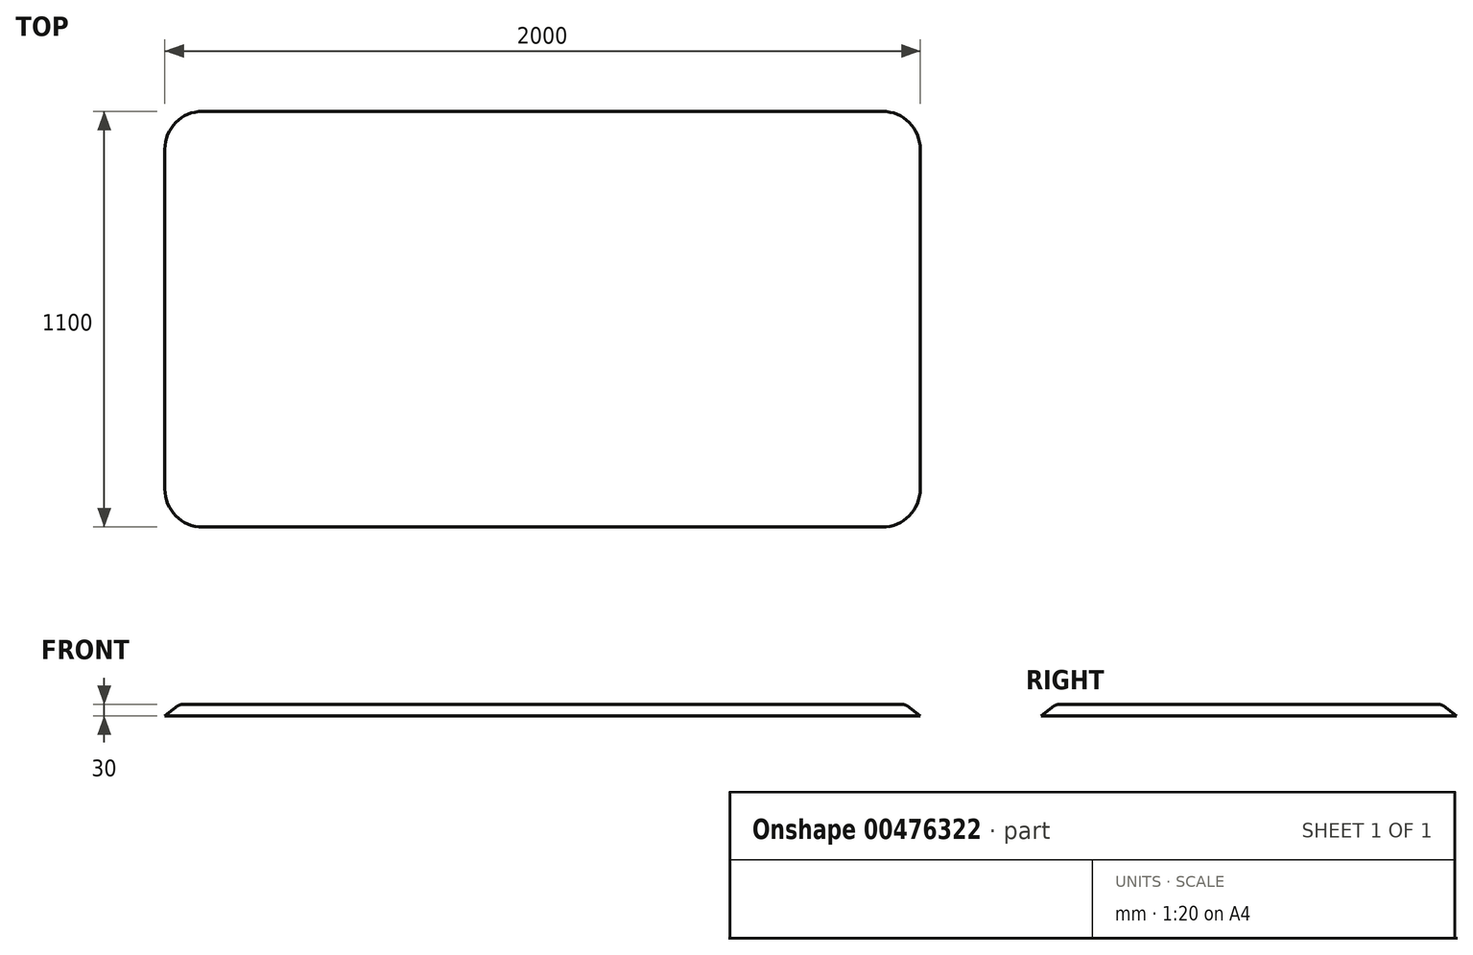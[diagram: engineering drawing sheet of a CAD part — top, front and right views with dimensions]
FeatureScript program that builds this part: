
annotation { "Feature Type Name" : "Feature", "Feature Type Description" : "" }
export const myFeature = defineFeature(function(context is Context, id is Id, definition is map)
    precondition{}
    {
        {
            var Q0;
            Q0=qCreatedBy(makeId("Top.planeOp"),FACE);
            var sketch = newSketch(context, id + "F0", { "sketchPlane" : qUnion([Q0])});
            skLineSegment(sketch, "E0.bottom", {"start": v(950, 500) * mm, "end": v(-950, 500) * mm});
            skLineSegment(sketch, "E0.top", {"start": v(950, -500) * mm, "end": v(-950, -500) * mm});
            skLineSegment(sketch, "E0.left", {"start": v(950, 500) * mm, "end": v(950, -500) * mm});
            skLineSegment(sketch, "E0.right", {"start": v(-950, 500) * mm, "end": v(-950, -500) * mm});
            skPoint(sketch, "E0.middle", {"position": v(0, 0) * mm});
            skSolve(sketch);
        }
        {
            var Q0;
            Q0=qSketchRegion(id+"F0",true);
            extrude(context, id + "F1", {"entities" : qUnion([Q0]), "depth" : 30 * mm});
        }
        {
            var Q0;
            Q0=makeQuery(id+"F1.opExtrude","SWEPT_EDGE",EDGE,{"disambiguationData":[OSD([sQuery(id+"F0.wireOp",EDGE,"E0.top"),sQuery(id+"F0.wireOp",EDGE,"E0.right")])]});
            var Q1;
            Q1=makeQuery(id+"F1.opExtrude","SWEPT_EDGE",EDGE,{"disambiguationData":[OSD([sQuery(id+"F0.wireOp",EDGE,"E0.bottom"),sQuery(id+"F0.wireOp",EDGE,"E0.right")])]});
            var Q2;
            Q2=makeQuery(id+"F1.opExtrude","SWEPT_EDGE",EDGE,{"disambiguationData":[OSD([sQuery(id+"F0.wireOp",EDGE,"E0.top"),sQuery(id+"F0.wireOp",EDGE,"E0.left")])]});
            var Q3;
            Q3=makeQuery(id+"F1.opExtrude","SWEPT_EDGE",EDGE,{"disambiguationData":[OSD([sQuery(id+"F0.wireOp",EDGE,"E0.bottom"),sQuery(id+"F0.wireOp",EDGE,"E0.left")])]});
            fillet(context, id + "F2", {"entities" : qUnion([Q0, Q1, Q2, Q3]), "radius" : 50 * mm, "tangentPropagation" : true, "allowEdgeOverflow" : false});
        }
        {
            var Q0;
            Q0=makeQuery(id+"F1.opExtrude","SWEPT_FACE",FACE,{"disambiguationData":[OSD([sQuery(id+"F0.wireOp",EDGE,"E0.top")])]});
            cPlane(context, id + "F3", {"entities" : qUnion([Q0]), "cplaneType" : CPlaneType.OFFSET, "offset" : 50 * mm, "oppositeDirection" : true, "width" : 152.4 * mm, "height" : 152.4 * mm});
        }
        {
            var Q0;
            Q0=qCreatedBy(id+"F3.planeOp",FACE);
            var sketch = newSketch(context, id + "F4", { "sketchPlane" : qUnion([Q0])});
            skPoint(sketch, "E1.0", {"position": v(950, 30) * mm});
            skPoint(sketch, "E2.0", {"position": v(950, 0) * mm});
            skLineSegment(sketch, "E3.0", {"start": v(950, 30) * mm, "end": v(950, 0) * mm});
            skLineSegment(sketch, "E4.top", {"start": v(950, 0) * mm, "end": v(1000, 0) * mm, "construction": true});
            skLineSegment(sketch, "E4.left", {"start": v(950, 30) * mm, "end": v(950, 0) * mm, "construction": true});
            skLineSegment(sketch, "E4.right", {"start": v(1000, 30) * mm, "end": v(1000, 0) * mm, "construction": true});
            skLineSegment(sketch, "E5", {"start": v(950, 30) * mm, "end": v(953.33, 30) * mm});
            skLineSegment(sketch, "E6", {"start": v(965.33, 26) * mm, "end": v(1000, 0) * mm});
            skPoint(sketch, "E7.visualSharp", {"position": v(960, 30) * mm});
            skArc(sketch, "E7.filletArc", {"start": v(965.33, 26) * mm, "mid": v(959.66, 28.97) * mm, "end": v(953.33, 30) * mm});
            skLineSegment(sketch, "E8", {"start": v(1000, 0) * mm, "end": v(950, 0) * mm});
            skSolve(sketch);
        }
        {
            var Q0;
            Q0=makeQuery(id+"F1.opExtrude","CAP_FACE",FACE,{"disambiguationData":[OSD([sQuery(id+"F0.wireOp",EDGE,"E0.bottom"),sQuery(id+"F0.wireOp",EDGE,"E0.top"),sQuery(id+"F0.wireOp",EDGE,"E0.left"),sQuery(id+"F0.wireOp",EDGE,"E0.right")])],"isStart":false});
            var sketch = newSketch(context, id + "F5", { "sketchPlane" : qUnion([Q0])});
            skLineSegment(sketch, "E9.0.0", {"start": v(900, 500) * mm, "end": v(-900, 500) * mm});
            skArc(sketch, "E9.0.1", {"start": v(-900, 500) * mm, "mid": v(-935.36, 485.36) * mm, "end": v(-950, 450) * mm});
            skLineSegment(sketch, "E9.0.2", {"start": v(-950, 450) * mm, "end": v(-950, -450) * mm});
            skArc(sketch, "E9.0.3", {"start": v(-950, -450) * mm, "mid": v(-935.36, -485.36) * mm, "end": v(-900, -500) * mm});
            skLineSegment(sketch, "E9.0.4", {"start": v(-900, -500) * mm, "end": v(900, -500) * mm});
            skArc(sketch, "E9.0.5", {"start": v(900, -500) * mm, "mid": v(935.36, -485.36) * mm, "end": v(950, -450) * mm});
            skLineSegment(sketch, "E9.0.6", {"start": v(950, -450) * mm, "end": v(950, 450) * mm});
            skArc(sketch, "E9.0.7", {"start": v(950, 450) * mm, "mid": v(935.36, 485.36) * mm, "end": v(900, 500) * mm});
            skSolve(sketch);
        }
        {
            var Q0;
            Q0=makeQuery(id+"F4.imprint","IMPRINT",FACE,{"disambiguationData":[TD([[makeQuery(id+"F4.imprint","IMPRINT",EDGE,{"derivedFrom":sQuery(id+"F4.wireOp",EDGE,"E5")}),-1.0]])]});
            var Q1;
            Q1 = qConstructionFilter(qBodyType(qCreatedBy(id + "F5" ,EDGE), BodyType.WIRE), ConstructionObject.NO);
            sweep(context, id + "F6", {"operationType" : NewBodyOperationType.ADD, "profiles" : qUnion([Q0]), "path" : qUnion([Q1])});
        }
    });
